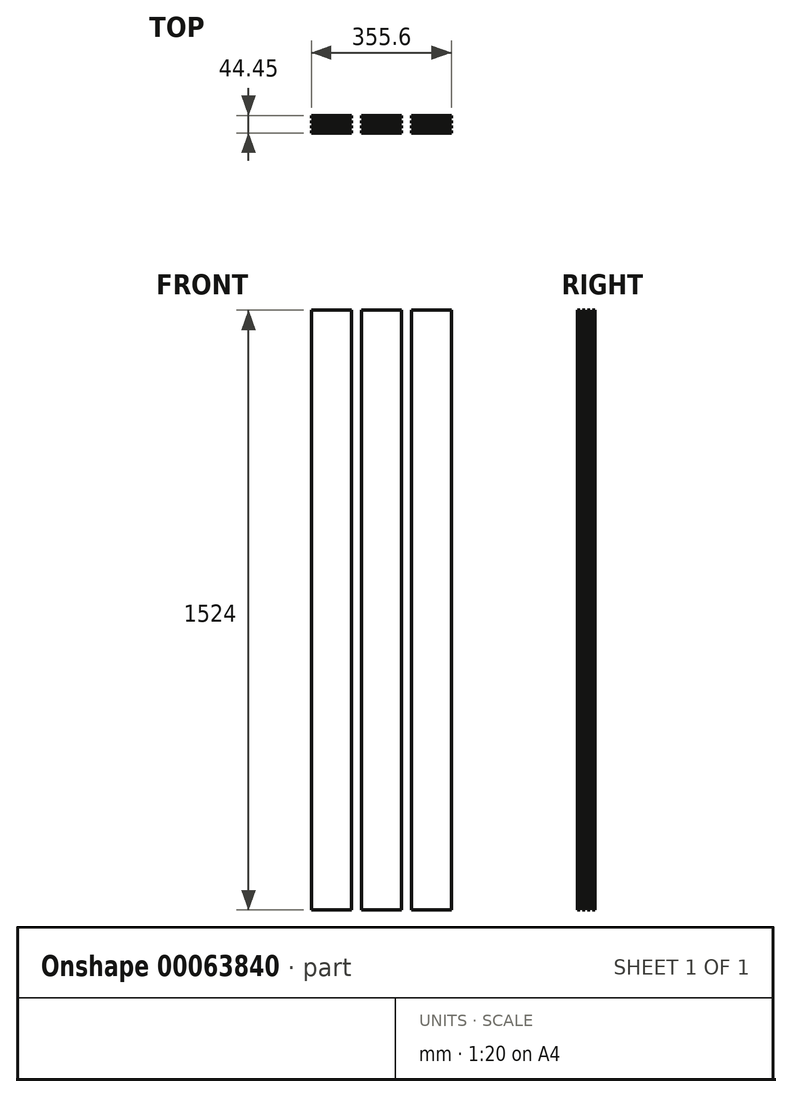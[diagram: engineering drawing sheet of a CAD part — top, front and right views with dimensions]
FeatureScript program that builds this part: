
annotation { "Feature Type Name" : "Feature", "Feature Type Description" : "" }
export const myFeature = defineFeature(function(context is Context, id is Id, definition is map)
    precondition{}
    {
        {
            var Q0;
            Q0=qCreatedBy(makeId("Top.planeOp"),FACE);
            var sketch = newSketch(context, id + "F0", { "sketchPlane" : qUnion([Q0])});
            skLineSegment(sketch, "E0.bottom", {"start": v(0, 0) * mm, "end": v(101.6, 0) * mm});
            skLineSegment(sketch, "E0.top", {"start": v(0, 6.35) * mm, "end": v(101.6, 6.35) * mm});
            skLineSegment(sketch, "E0.left", {"start": v(0, 0) * mm, "end": v(0, 6.35) * mm});
            skLineSegment(sketch, "E0.right", {"start": v(101.6, 0) * mm, "end": v(101.6, 6.35) * mm});
            skLineSegment(sketch, "E1.0.1.0", {"start": v(0, 19.05) * mm, "end": v(101.6, 19.05) * mm});
            skLineSegment(sketch, "E1.0.1.1", {"start": v(0, 12.7) * mm, "end": v(0, 19.05) * mm});
            skLineSegment(sketch, "E1.0.1.2", {"start": v(101.6, 12.7) * mm, "end": v(101.6, 19.05) * mm});
            skLineSegment(sketch, "E1.0.1.3", {"start": v(0, 12.7) * mm, "end": v(101.6, 12.7) * mm});
            skLineSegment(sketch, "E1.0.2.0", {"start": v(0, 31.75) * mm, "end": v(101.6, 31.75) * mm});
            skLineSegment(sketch, "E1.0.2.1", {"start": v(0, 25.4) * mm, "end": v(0, 31.75) * mm});
            skLineSegment(sketch, "E1.0.2.2", {"start": v(101.6, 25.4) * mm, "end": v(101.6, 31.75) * mm});
            skLineSegment(sketch, "E1.0.2.3", {"start": v(0, 25.4) * mm, "end": v(101.6, 25.4) * mm});
            skLineSegment(sketch, "E1.0.3.0", {"start": v(0, 44.45) * mm, "end": v(101.6, 44.45) * mm});
            skLineSegment(sketch, "E1.0.3.1", {"start": v(0, 38.1) * mm, "end": v(0, 44.45) * mm});
            skLineSegment(sketch, "E1.0.3.2", {"start": v(101.6, 38.1) * mm, "end": v(101.6, 44.45) * mm});
            skLineSegment(sketch, "E1.0.3.3", {"start": v(0, 38.1) * mm, "end": v(101.6, 38.1) * mm});
            skLineSegment(sketch, "E1.1.0.0", {"start": v(127, 6.35) * mm, "end": v(228.6, 6.35) * mm});
            skLineSegment(sketch, "E1.1.0.1", {"start": v(127, 0) * mm, "end": v(127, 6.35) * mm});
            skLineSegment(sketch, "E1.1.0.2", {"start": v(228.6, 0) * mm, "end": v(228.6, 6.35) * mm});
            skLineSegment(sketch, "E1.1.0.3", {"start": v(127, 0) * mm, "end": v(228.6, 0) * mm});
            skLineSegment(sketch, "E1.1.1.0", {"start": v(127, 19.05) * mm, "end": v(228.6, 19.05) * mm});
            skLineSegment(sketch, "E1.1.1.1", {"start": v(127, 12.7) * mm, "end": v(127, 19.05) * mm});
            skLineSegment(sketch, "E1.1.1.2", {"start": v(228.6, 12.7) * mm, "end": v(228.6, 19.05) * mm});
            skLineSegment(sketch, "E1.1.1.3", {"start": v(127, 12.7) * mm, "end": v(228.6, 12.7) * mm});
            skLineSegment(sketch, "E1.1.2.0", {"start": v(127, 31.75) * mm, "end": v(228.6, 31.75) * mm});
            skLineSegment(sketch, "E1.1.2.1", {"start": v(127, 25.4) * mm, "end": v(127, 31.75) * mm});
            skLineSegment(sketch, "E1.1.2.2", {"start": v(228.6, 25.4) * mm, "end": v(228.6, 31.75) * mm});
            skLineSegment(sketch, "E1.1.2.3", {"start": v(127, 25.4) * mm, "end": v(228.6, 25.4) * mm});
            skLineSegment(sketch, "E1.1.3.0", {"start": v(127, 44.45) * mm, "end": v(228.6, 44.45) * mm});
            skLineSegment(sketch, "E1.1.3.1", {"start": v(127, 38.1) * mm, "end": v(127, 44.45) * mm});
            skLineSegment(sketch, "E1.1.3.2", {"start": v(228.6, 38.1) * mm, "end": v(228.6, 44.45) * mm});
            skLineSegment(sketch, "E1.1.3.3", {"start": v(127, 38.1) * mm, "end": v(228.6, 38.1) * mm});
            skLineSegment(sketch, "E1.2.0.0", {"start": v(254, 6.35) * mm, "end": v(355.6, 6.35) * mm});
            skLineSegment(sketch, "E1.2.0.1", {"start": v(254, 0) * mm, "end": v(254, 6.35) * mm});
            skLineSegment(sketch, "E1.2.0.2", {"start": v(355.6, 0) * mm, "end": v(355.6, 6.35) * mm});
            skLineSegment(sketch, "E1.2.0.3", {"start": v(254, 0) * mm, "end": v(355.6, 0) * mm});
            skLineSegment(sketch, "E1.2.1.0", {"start": v(254, 19.05) * mm, "end": v(355.6, 19.05) * mm});
            skLineSegment(sketch, "E1.2.1.1", {"start": v(254, 12.7) * mm, "end": v(254, 19.05) * mm});
            skLineSegment(sketch, "E1.2.1.2", {"start": v(355.6, 12.7) * mm, "end": v(355.6, 19.05) * mm});
            skLineSegment(sketch, "E1.2.1.3", {"start": v(254, 12.7) * mm, "end": v(355.6, 12.7) * mm});
            skLineSegment(sketch, "E1.2.2.0", {"start": v(254, 31.75) * mm, "end": v(355.6, 31.75) * mm});
            skLineSegment(sketch, "E1.2.2.1", {"start": v(254, 25.4) * mm, "end": v(254, 31.75) * mm});
            skLineSegment(sketch, "E1.2.2.2", {"start": v(355.6, 25.4) * mm, "end": v(355.6, 31.75) * mm});
            skLineSegment(sketch, "E1.2.2.3", {"start": v(254, 25.4) * mm, "end": v(355.6, 25.4) * mm});
            skLineSegment(sketch, "E1.2.3.0", {"start": v(254, 44.45) * mm, "end": v(355.6, 44.45) * mm});
            skLineSegment(sketch, "E1.2.3.1", {"start": v(254, 38.1) * mm, "end": v(254, 44.45) * mm});
            skLineSegment(sketch, "E1.2.3.2", {"start": v(355.6, 38.1) * mm, "end": v(355.6, 44.45) * mm});
            skLineSegment(sketch, "E1.2.3.3", {"start": v(254, 38.1) * mm, "end": v(355.6, 38.1) * mm});
            skLineSegment(sketch, "E1.direction1", {"start": v(0, 6.35) * mm, "end": v(127, 6.35) * mm, "construction": true});
            skLineSegment(sketch, "E1.direction2", {"start": v(0, 6.35) * mm, "end": v(0, 19.05) * mm, "construction": true});
            skSolve(sketch);
        }
        {
            var Q0;
            Q0 = qSketchRegion(id + "F0", true);
            extrude(context, id + "F1", {"entities" : qUnion([Q0]), "endBound" : BoundingType.SYMMETRIC, "depth" : 1524 * mm});
        }
    });
